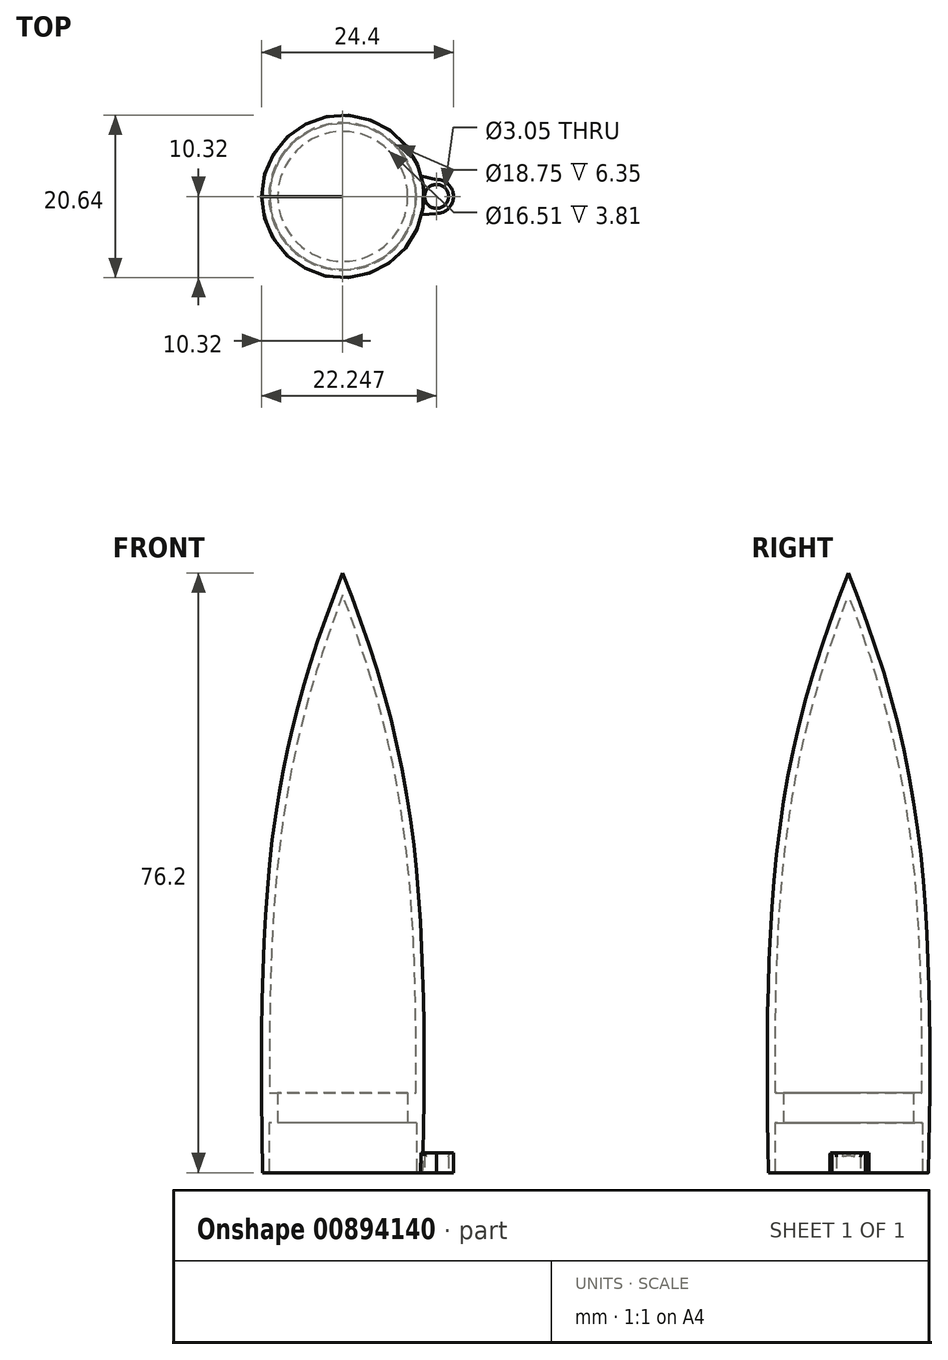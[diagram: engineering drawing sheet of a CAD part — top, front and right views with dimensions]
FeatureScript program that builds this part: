
annotation { "Feature Type Name" : "Feature", "Feature Type Description" : "" }
export const myFeature = defineFeature(function(context is Context, id is Id, definition is map)
    precondition{}
    {
        {
            var Q0;
            Q0=qCreatedBy(makeId("Front.planeOp"),FACE);
            var sketch = newSketch(context, id + "F0", { "sketchPlane" : qUnion([Q0])});
            skLineSegment(sketch, "E0", {"start": v(0, 0) * mm, "end": v(-10.16, 0) * mm});
            skLineSegment(sketch, "E1", {"start": v(0, 0) * mm, "end": v(0, 76.2) * mm});
            skFitSpline(sketch, "E2", {"points": [v(0, 76.2) * mm, v(-10.16, 0) * mm], "startDerivative": vector(-26.98, -69.08) * mm, "endDerivative": vector(2.43, -114.26) * mm});
            skSolve(sketch);
        }
        {
            var Q0;
            Q0=makeQuery(id+"F0.imprint","IMPRINT",FACE,{"disambiguationData":[TD([[makeQuery(id+"F0.imprint","IMPRINT",EDGE,{"derivedFrom":sQuery(id+"F0.wireOp",EDGE,"E0")}),-1.0]])]});
            var Q1;
            Q1=sQuery(id+"F0.wireOp",EDGE,"E1");
            revolve(context, id + "F1", {"surfaceOperationType" : NewSurfaceOperationType.NEW, "entities" : qUnion([Q0]), "axis" : qUnion([Q1]), "revolveType" : RevolveType.FULL});
        }
        {
            var Q0;
            Q0=makeQuery(id+"F1.opRevolve","SWEPT_FACE",FACE,{"disambiguationData":[OSD([sQuery(id+"F0.wireOp",EDGE,"E0")])]});
            shell(context, id + "F2", {"entities" : qUnion([Q0]), "thickness" : 1.02 * mm});
        }
        {
            var Q0;
            Q0=qCreatedBy(makeId("Top.planeOp"),FACE);
            var sketch = newSketch(context, id + "F3", { "sketchPlane" : qUnion([Q0])});
            skCircle(sketch, "E3", {"center": v(11.93, 0) * mm, "radius": 1.52 * mm});
            skCircle(sketch, "E4", {"center": v(11.93, 0) * mm, "radius": 2.15 * mm});
            skLineSegment(sketch, "E5", {"start": v(11.93, 2.15) * mm, "end": v(9.25, 2.73) * mm});
            skLineSegment(sketch, "E6", {"start": v(9.25, 2.73) * mm, "end": v(9.25, -2.4) * mm});
            skLineSegment(sketch, "E7", {"start": v(9.25, -2.4) * mm, "end": v(11.93, -2.16) * mm});
            skLineSegment(sketch, "E8", {"start": v(11.93, -2.16) * mm, "end": v(11.94, -2.15) * mm});
            skSolve(sketch);
        }
        {
            var Q0;
            {var subQ0=sQuery(id+"F3.wireOp",EDGE,"E5");Q0=makeQuery(id+"F3.imprint","IMPRINT",FACE,{"disambiguationData":[TD([[makeQuery(id+"F3.imprint","IMPRINT",EDGE,{"derivedFrom":subQ0}),1.0]])]});}
            var Q1;
            Q1=makeQuery(id+"F3.imprint","IMPRINT",FACE,{"disambiguationData":[TD([[makeQuery(id+"F3.imprint","IMPRINT",EDGE,{"derivedFrom":sQuery(id+"F3.wireOp",EDGE,"E3")}),-1.0]])]});
            extrude(context, id + "F4", {"entities" : qUnion([Q0, Q1]), "operationType" : NewBodyOperationType.ADD, "depth" : 2.54 * mm, "offsetDistance" : 25.4 * mm});
        }
        {
            var Q0;
            Q0=makeQuery(id+"F4.opExtrude","CAP_EDGE",EDGE,{"disambiguationData":[OSD([sQuery(id+"F3.wireOp",EDGE,"E3")])],"isStart":false});
            fillet(context, id + "F5", {"entities" : qUnion([Q0]), "radius" : 0.5 * mm, "tangentPropagation" : true, "allowEdgeOverflow" : false});
        }
        {
            var Q0;
            Q0=qCreatedBy(makeId("Top.planeOp"),FACE);
            var sketch = newSketch(context, id + "F6", { "sketchPlane" : qUnion([Q0])});
            skCircle(sketch, "E9", {"center": v(0, 0) * mm, "radius": 9.38 * mm});
            skCircle(sketch, "E10", {"center": v(0, 0) * mm, "radius": 8.25 * mm});
            skSolve(sketch);
        }
        {
            var Q0;
            Q0=makeQuery(id+"F6.imprint","IMPRINT",FACE,{"disambiguationData":[TD([[makeQuery(id+"F6.imprint","IMPRINT",EDGE,{"derivedFrom":sQuery(id+"F6.wireOp",EDGE,"E9")}),1.0]])]});
            extrude(context, id + "F7", {"entities" : qUnion([Q0]), "operationType" : NewBodyOperationType.ADD, "depth" : 10.16 * mm, "offsetDistance" : 25.4 * mm});
        }
        {
            var Q0;
            Q0=makeQuery(id+"F6.imprint","IMPRINT",FACE,{"disambiguationData":[TD([[makeQuery(id+"F6.imprint","IMPRINT",EDGE,{"derivedFrom":sQuery(id+"F6.wireOp",EDGE,"E9")}),1.0]])]});
            extrude(context, id + "F8", {"entities" : qUnion([Q0]), "operationType" : NewBodyOperationType.REMOVE, "depth" : 6.35 * mm, "offsetDistance" : 25.4 * mm});
        }
    });
